# Revit family: Haworth_Belong_Tool_TerritoryScreen
name_source: partatom
category: Furniture Systems
revit_build: Autodesk Revit 2018 (Build: 20170223_1515(x64)
units: mm (PartAtom-declared; Revit-internal decimal feet)

## family parameters
Always vertical = Yes
Cut with Voids When Loaded = No
OmniClass Number = 23.40.70.14.64.21
OmniClass Title = Systems Furniture
Part Type = Normal
Room Calculation Point = No
Round Connector Dimension = Use Diameter
Shared = No
Work Plane-Based = No

## types (2) — shared parameters
Actual Height = 12"
Actual Mounting Height = 29"
Actual Width = 23 3/4"
Assembly Code = E2020200
Bracket Finish = Haworth _ Metal _ Brushed Aluminum
Bracket Offset = 3"
Bracket Spacing = 13 3/4"
Custom Size = No
Description = Haworth - Belong Screen - Territory
Height = 12"
Manufacturer = Haworth
Max. Height = 12"
Max. Width = 23 3/4"
Min. Height = 12"
Min. Width = 24"
Model = Haworth - Belong Screen - Territory
Panel Bottom Offset = 1/4"
Revision Number = 4
Screen Depth = 11/128"
Screen Finish = Haworth _ Polymer _ Snow
Size = Verify Final Dim. w/ Haworth
Standard Heights = 12 in.
Standard Widths = 24 in.
Territory Screen = Yes
URL = www.haworth.com
URL - Product = http://www.haworth.com
Warranty = http://www.haworth.com
Width = 24"
Worksurface Height = 29"
Worksurface Thickness = 1 3/16"

## per-type parameters (varying)
| type | Sustainability Info |
| Territory Screen Shared | http://www.haworth.com |
| Territory Screen End | https://www.haworth.com |

type visibility flags: 2 boolean params named "<type name>" — each type sets only its own to Yes (folded from table)

## geometry (parser evidence)
native form markers: Sweep x3
no freeform markers — native parametric forms only
